# Revit family: AFX-Gale-Outdoor_Sconce+
name_source: partatom
category: Lighting Fixtures
units: mm (PartAtom-declared; Revit-internal decimal feet)

## family parameters
Cut with Voids When Loaded = No
Host = Face
Light Source = Yes
Part Type = Normal
Room Calculation Point = No
Round Connector Dimension = Use Diameter
Shared = No

## types (6) — shared parameters
Apparent Load = 120 VA
Assembly Code = E2020200
Color Filter = 16777215
Colour Rendering Index = 90
Default Elevation = 48"
Depth = 2 1/2"
Diffuser Finish = AFX - White Acrylic
Dimming Lamp Color Temperature Shift = <None>
Emit Shape Visible in Rendering = No
Emit from Rectangle Width = 1 13/16"
Keynote = 12500
Lamp = LED
Manufacturer = AFX Inc
Product Documentation Link = https://www.afxinc.com
Revit Model Built By = https://servex-us.com
Tilt Angle = -90.00°
Type Comments = Gale
URL = https://www.afxinc.com
Voltage = 120 V
Width = 4 1/2"

## per-type parameters (varying)
| type | Base Finish | Body Finish | Description | Emit from Rectangle Length | Height | Height Base | Photometric Web File | Wattage Comments |
| GLEW0518L30UDBK | AFX - Black Steel | AFX - Black Steel | LED Outdoor Sconce - 4 1/2"W x 2 1/2"D x 18"H | 17 3/8" | 18" | 6 3/4" | GLEW0518L30UDxx_IES.IES | 25W |
| GLEW0524L30UDBK | AFX - Black Steel | AFX - Black Steel | LED Outdoor Sconce - 4 1/2"W x 2 1/2"D x 24"H | 23 3/8" | 24" | 13 1/2" | GLEW0524L30UDxx_IES.IES | 29W |
| GLEW0536L30UDBK | AFX - Black Steel | AFX - Black Steel | LED Outdoor Sconce - 4 1/2"W x 2 1/2"D x 36"H | 35 3/8" | 36" | 13 1/2" | GLEW0536L30UDxx_IES.IES | 35W |
| GLEW0518L30UDTG | AFX - Textured Grey | AFX - Textured Grey | LED Outdoor Sconce - 4 1/2"W x 2 1/2"D x 18"H | 17 3/8" | 18" | 6 3/4" | GLEW0518L30UDxx_IES.IES | 25W |
| GLEW0524L30UDTG | AFX - Textured Grey | AFX - Textured Grey | LED Outdoor Sconce - 4 1/2"W x 2 1/2"D x 24"H | 23 3/8" | 24" | 13 1/2" | GLEW0524L30UDxx_IES.IES | 29W |
| GLEW0536L30UDTG | AFX - Textured Grey | AFX - Textured Grey | LED Outdoor Sconce - 4 1/2"W x 2 1/2"D x 36"H | 35 3/8" | 36" | 13 1/2" | GLEW0536L30UDxx_IES.IES | 35W |

note: column(s) folded — value = type name in every type: Model

## geometry (parser evidence)
native form markers: Sweep x2
no freeform markers — native parametric forms only
